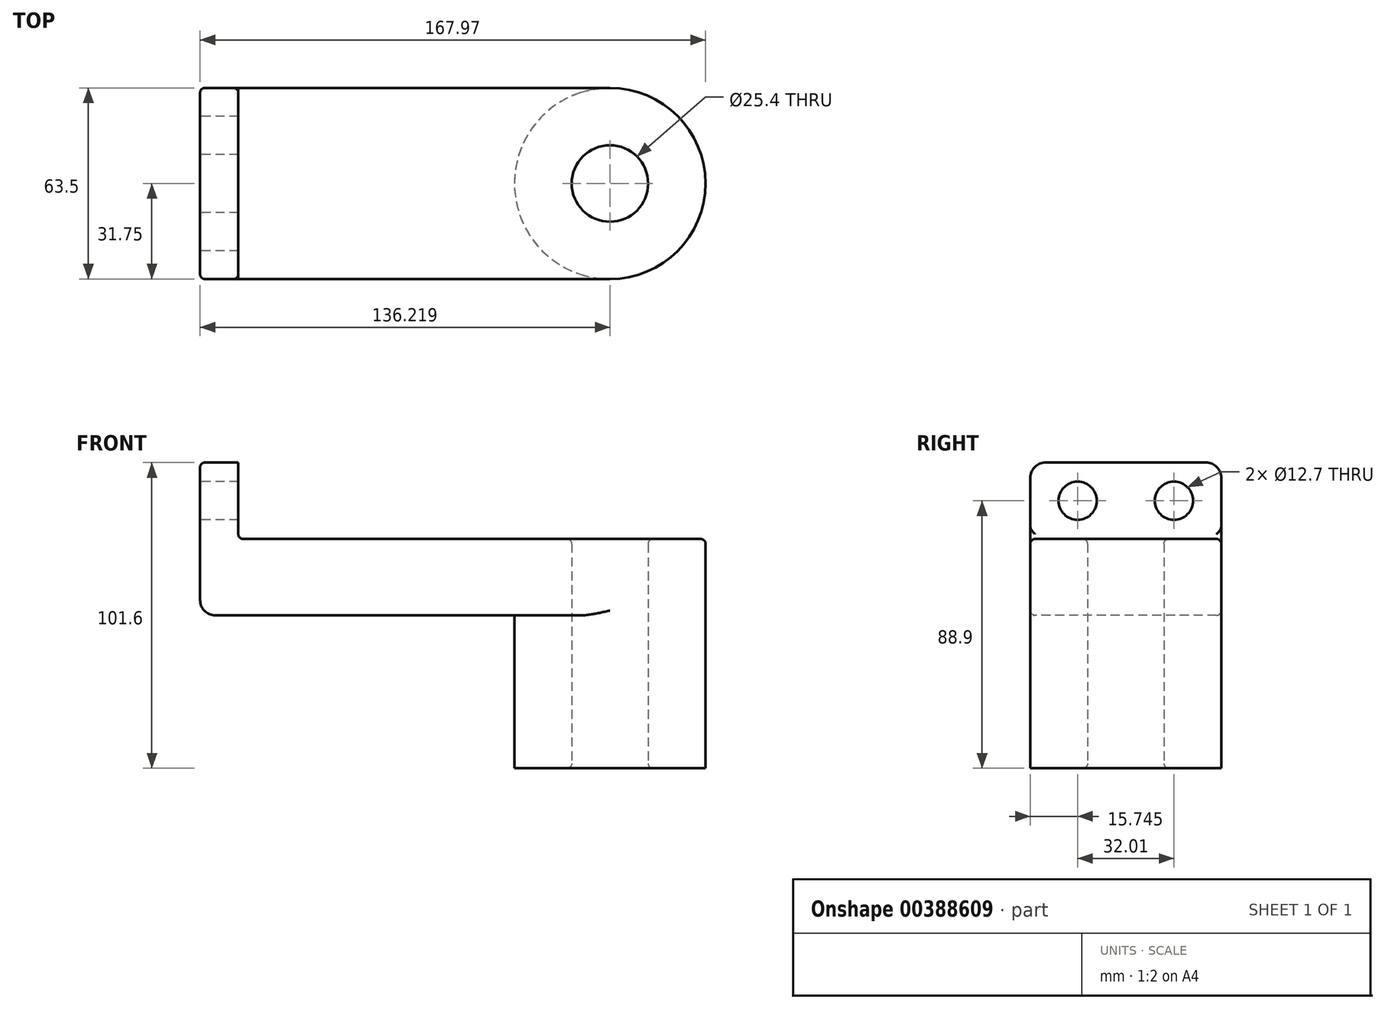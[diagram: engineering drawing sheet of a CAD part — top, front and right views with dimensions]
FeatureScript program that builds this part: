
annotation { "Feature Type Name" : "Feature", "Feature Type Description" : "" }
export const myFeature = defineFeature(function(context is Context, id is Id, definition is map)
    precondition{}
    {
        {
            var Q0;
            Q0=qCreatedBy(makeId("Top.planeOp"),FACE);
            var sketch = newSketch(context, id + "F0", { "sketchPlane" : qUnion([Q0])});
            skLineSegment(sketch, "E0.bottom", {"start": v(-68.1, 31.75) * mm, "end": v(68.1, 31.75) * mm});
            skLineSegment(sketch, "E0.top", {"start": v(-68.1, -31.75) * mm, "end": v(68.1, -31.75) * mm});
            skLineSegment(sketch, "E0.left", {"start": v(-68.1, 31.75) * mm, "end": v(-68.1, -31.75) * mm});
            skLineSegment(sketch, "E0.right", {"start": v(68.1, 31.75) * mm, "end": v(68.1, -31.75) * mm});
            skPoint(sketch, "E0.middle", {"position": v(0, 0) * mm});
            skCircle(sketch, "E1", {"center": v(68.1, 0) * mm, "radius": 31.75 * mm});
            skCircle(sketch, "E2", {"center": v(68.1, 0) * mm, "radius": 12.7 * mm});
            skSolve(sketch);
        }
        {
            var Q0;
            {var subQ1=sQuery(id+"F0.wireOp",EDGE,"E0.right");var subQ3=sQuery(id+"F0.wireOp",EDGE,"E2");var subQ4=makeQuery(id+"F0.imprint","INTERSECT",VERTEX,{"disambiguationData":[OD(0.0)],"derivedFrom":[subQ1,subQ3]});Q0=makeQuery(id+"F0.imprint","IMPRINT",FACE,{"disambiguationData":[TD([[makeQuery(id+"F0.imprint","IMPRINT",EDGE,{"disambiguationData":[TD([[subQ4,1.0]])],"derivedFrom":subQ3}),-1.0]])]});}
            var Q1;
            {var subQ1=sQuery(id+"F0.wireOp",EDGE,"E0.right");var subQ3=sQuery(id+"F0.wireOp",EDGE,"E2");var subQ4=makeQuery(id+"F0.imprint","INTERSECT",VERTEX,{"disambiguationData":[OD(0.0)],"derivedFrom":[subQ1,subQ3]});Q1=makeQuery(id+"F0.imprint","IMPRINT",FACE,{"disambiguationData":[TD([[makeQuery(id+"F0.imprint","IMPRINT",EDGE,{"disambiguationData":[TD([[subQ4,-1.0]])],"derivedFrom":subQ3}),-1.0]])]});}
            var Q2;
            {var subQ0=sQuery(id+"F0.wireOp",EDGE,"E0.bottom");Q2=makeQuery(id+"F0.imprint","IMPRINT",FACE,{"disambiguationData":[TD([[makeQuery(id+"F0.imprint","IMPRINT",EDGE,{"derivedFrom":subQ0}),-1.0]])]});}
            extrude(context, id + "F1", {"entities" : qUnion([Q0, Q1, Q2]), "depth" : 25.4 * mm});
        }
        {
            var Q0;
            {var subQ1=sQuery(id+"F0.wireOp",EDGE,"E0.right");var subQ3=sQuery(id+"F0.wireOp",EDGE,"E2");var subQ4=makeQuery(id+"F0.imprint","INTERSECT",VERTEX,{"disambiguationData":[OD(0.0)],"derivedFrom":[subQ1,subQ3]});Q0=makeQuery(id+"F0.imprint","IMPRINT",FACE,{"disambiguationData":[TD([[makeQuery(id+"F0.imprint","IMPRINT",EDGE,{"disambiguationData":[TD([[subQ4,-1.0]])],"derivedFrom":subQ3}),-1.0]])]});}
            var Q1;
            {var subQ1=sQuery(id+"F0.wireOp",EDGE,"E0.right");var subQ3=sQuery(id+"F0.wireOp",EDGE,"E2");var subQ4=makeQuery(id+"F0.imprint","INTERSECT",VERTEX,{"disambiguationData":[OD(0.0)],"derivedFrom":[subQ1,subQ3]});Q1=makeQuery(id+"F0.imprint","IMPRINT",FACE,{"disambiguationData":[TD([[makeQuery(id+"F0.imprint","IMPRINT",EDGE,{"disambiguationData":[TD([[subQ4,1.0]])],"derivedFrom":subQ3}),-1.0]])]});}
            extrude(context, id + "F2", {"entities" : qUnion([Q0, Q1]), "operationType" : NewBodyOperationType.ADD, "oppositeDirection" : true, "depth" : 50.8 * mm});
        }
        {
            var Q0;
            Q0=makeQuery(id+"F1.opExtrude","SWEPT_FACE",FACE,{"disambiguationData":[OSD([sQuery(id+"F0.wireOp",EDGE,"E0.left")])]});
            var sketch = newSketch(context, id + "F3", { "sketchPlane" : qUnion([Q0])});
            skLineSegment(sketch, "E3.bottom", {"start": v(31.75, 0) * mm, "end": v(-31.75, 0) * mm});
            skLineSegment(sketch, "E3.top", {"start": v(31.75, 50.8) * mm, "end": v(-31.75, 50.8) * mm});
            skLineSegment(sketch, "E3.left", {"start": v(31.75, 0) * mm, "end": v(31.75, 50.8) * mm});
            skLineSegment(sketch, "E3.right", {"start": v(-31.75, 0) * mm, "end": v(-31.75, 50.8) * mm});
            skLineSegment(sketch, "E4", {"start": v(0, 25.4) * mm, "end": v(0, 50.8) * mm});
            skCircle(sketch, "E5", {"center": v(16, 38.1) * mm, "radius": 6.35 * mm});
            skCircle(sketch, "E6.MirrorC", {"center": v(-16, 38.1) * mm, "radius": 6.35 * mm});
            skSolve(sketch);
        }
        {
            var Q0;
            Q0 = qSketchRegion(id + "F3", true);
            extrude(context, id + "F4", {"entities" : qUnion([Q0]), "operationType" : NewBodyOperationType.ADD, "oppositeDirection" : true, "depth" : 12.7 * mm});
        }
        {
            var Q0;
            Q0=makeQuery(id+"F2.opExtrude","CAP_EDGE",EDGE,{"disambiguationData":[OSD([sQuery(id+"F0.wireOp",EDGE,"E1")])],"isStart":true});
            var Q1;
            Q1=makeQuery(id+"F1.opExtrude","CAP_EDGE",EDGE,{"disambiguationData":[OSD([sQuery(id+"F0.wireOp",EDGE,"E0.left")])],"isStart":true});
            var Q2;
            Q2=makeQuery(id+"F4.opExtrude","SWEPT_EDGE",EDGE,{"disambiguationData":[OSD([sQuery(id+"F3.wireOp",EDGE,"E3.top"),sQuery(id+"F3.wireOp",EDGE,"E3.left")])]});
            var Q3;
            Q3=makeQuery(id+"F4.opExtrude","SWEPT_EDGE",EDGE,{"disambiguationData":[OSD([sQuery(id+"F3.wireOp",EDGE,"E3.top"),sQuery(id+"F3.wireOp",EDGE,"E3.right")])]});
            fillet(context, id + "F5", {"entities" : qUnion([Q0, Q1, Q2, Q3]), "radius" : 5.08 * mm, "tangentPropagation" : true, "allowEdgeOverflow" : false});
        }
        {
            var Q0;
            Q0=makeQuery(id+"F1.opExtrude","CAP_EDGE",EDGE,{"disambiguationData":[OSD([sQuery(id+"F0.wireOp",EDGE,"E0.top")])],"isStart":true});
            var Q1;
            Q1=makeQuery(id+"F1.opExtrude","CAP_EDGE",EDGE,{"disambiguationData":[OSD([sQuery(id+"F0.wireOp",EDGE,"E0.top")])],"isStart":false});
            var Q2;
            Q2=makeQuery(id+"F4.boolean.opBoolean","INTERSECT",EDGE,{"derivedFrom":[makeQuery(id+"F1.opExtrude","CAP_FACE",FACE,{"disambiguationData":[OSD([sQuery(id+"F0.wireOp",EDGE,"E0.bottom"),sQuery(id+"F0.wireOp",EDGE,"E0.top"),sQuery(id+"F0.wireOp",EDGE,"E0.left"),sQuery(id+"F0.wireOp",EDGE,"E1"),sQuery(id+"F0.wireOp",EDGE,"E2")])],"isStart":false}),makeQuery(id+"F4.opExtrude","CAP_FACE",FACE,{"disambiguationData":[OSD([sQuery(id+"F3.wireOp",EDGE,"E3.bottom"),sQuery(id+"F3.wireOp",EDGE,"E3.top"),sQuery(id+"F3.wireOp",EDGE,"E3.left"),sQuery(id+"F3.wireOp",EDGE,"E3.right"),sQuery(id+"F3.wireOp",EDGE,"E5"),sQuery(id+"F3.wireOp",EDGE,"E6.MirrorC")])],"isStart":false})]});
            var Q3;
            {var subQ0=sQuery(id+"F0.wireOp",EDGE,"E2");Q3=makeQuery(id+"F2.boolean.opBoolean","MERGE",FACE,{"derivedFrom":[makeQuery(id+"F1.opExtrude","SWEPT_FACE",FACE,{"disambiguationData":[OSD([subQ0])]}),makeQuery(id+"F2.opExtrude","SWEPT_FACE",FACE,{"disambiguationData":[OSD([subQ0])]})]});}
            fillet(context, id + "F6", {"entities" : qUnion([Q0, Q1, Q2, Q3]), "radius" : 1.59 * mm, "tangentPropagation" : true, "allowEdgeOverflow" : false});
        }
    });
